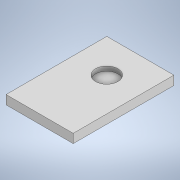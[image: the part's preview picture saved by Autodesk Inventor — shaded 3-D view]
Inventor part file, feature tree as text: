
AUTODESK INVENTOR PART (.ipt)
format: ipt  version: 2020 (Build 240168000, 168)  size: 100,864 bytes
history: native  units: mm
features: extrude x2, sketch x2
ambient origin geometry x8: Origin, YZ Plane, XZ Plane, XY Plane, X Axis, Y Axis, Z Axis, Center Point
bodies: Solid1 (feature_tree)
feature tree (4):
  extrude  "Extrusion1"  Depth=450.0mm
  extrude  "Extrusion2"  Depth=20.0mm
  sketch  "Sketch1"  dims[d0=300.0mm d1=450.0mm]
  sketch  "Sketch2"  dims[d2=40.0mm d3=0.0mm d4=150.0mm d5=150.0mm d6=100.0mm d7=20.0mm d8=0.0mm]
